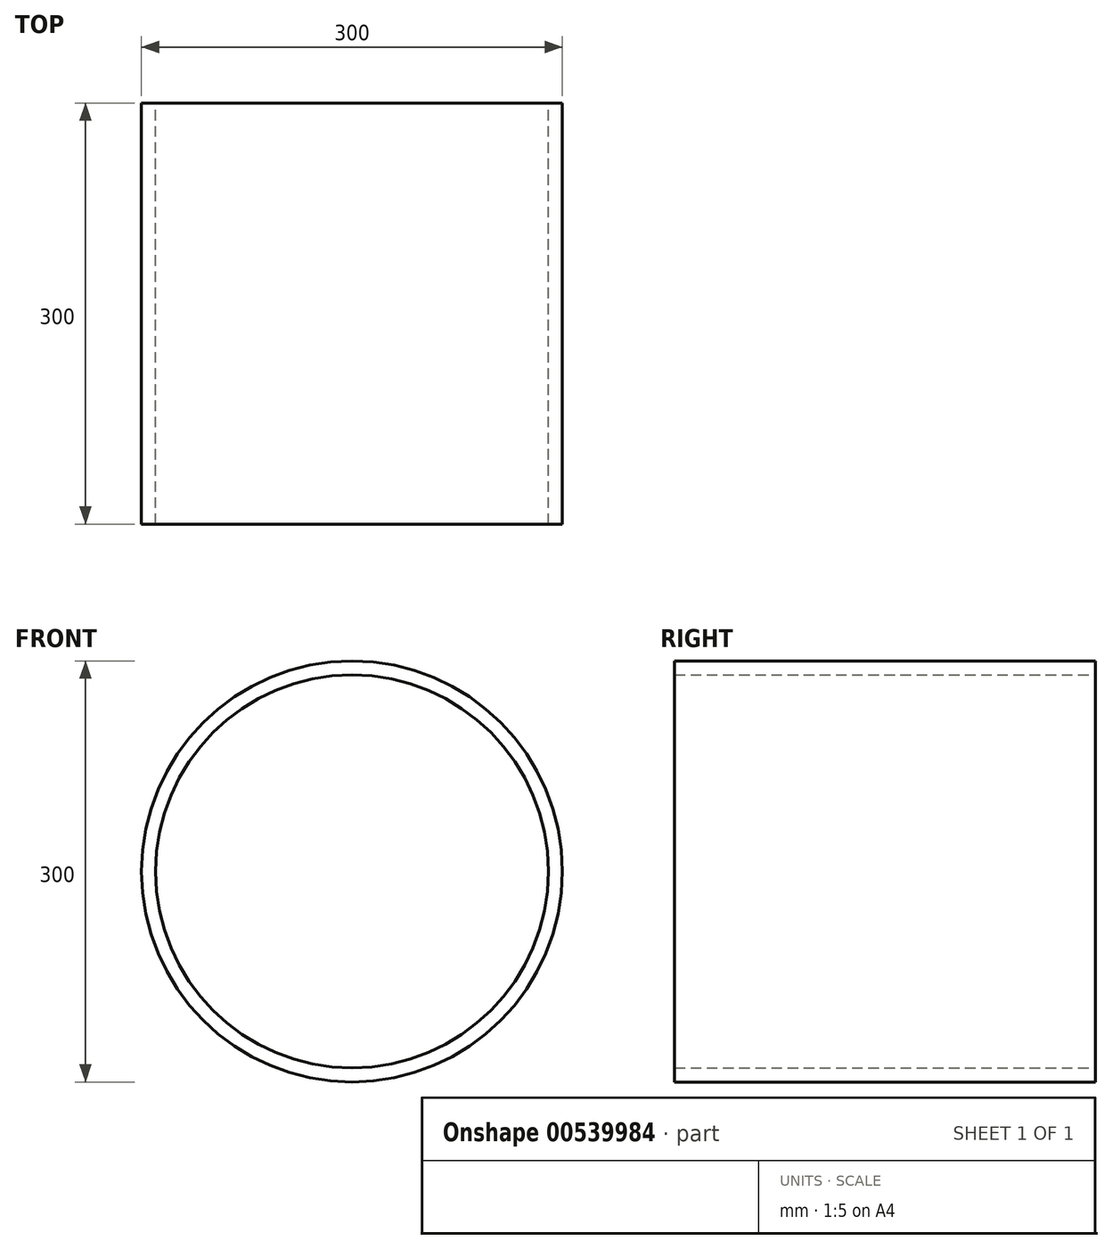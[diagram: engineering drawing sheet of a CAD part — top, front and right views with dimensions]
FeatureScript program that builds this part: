
annotation { "Feature Type Name" : "Feature", "Feature Type Description" : "" }
export const myFeature = defineFeature(function(context is Context, id is Id, definition is map)
    precondition{}
    {
        {
            var Q0;
            Q0=qCreatedBy(makeId("Front.planeOp"),FACE);
            var sketch = newSketch(context, id + "F0", { "sketchPlane" : qUnion([Q0])});
            skCircle(sketch, "E0", {"center": v(0, 0) * mm, "radius": 150 * mm});
            skCircle(sketch, "E1.0", {"center": v(0, 0) * mm, "radius": 140 * mm});
            skSolve(sketch);
        }
        {
            var Q0;
            Q0=makeQuery(id+"F0.imprint","IMPRINT",FACE,{"disambiguationData":[TD([[makeQuery(id+"F0.imprint","IMPRINT",EDGE,{"derivedFrom":sQuery(id+"F0.wireOp",EDGE,"E0")}),1.0]])]});
            extrude(context, id + "F1", {"entities" : qUnion([Q0]), "depth" : 300 * mm, "offsetDistance" : 25 * mm});
        }
    });
